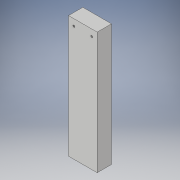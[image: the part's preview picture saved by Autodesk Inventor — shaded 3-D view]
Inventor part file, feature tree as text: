
AUTODESK INVENTOR PART (.ipt)
format: ipt  version: 2019 (Build 230136000, 136)  size: 103,936 bytes
history: native  units: in
note: dims shown in document units (in); Inventor stores cm internally (conversion verified against a paired STEP export)
features: sketch x2, extrude x1, hole x1
ambient origin geometry x8: Origin, YZ Plane, XZ Plane, XY Plane, X Axis, Y Axis, Z Axis, Center Point
bodies: Solid1 (feature_tree)
feature tree (4):
  extrude  "Extrusion1"  Depth=4.25in
  hole  "Hole1"  [1 undecoded]
  sketch  "Sketch1"  dims[d0=1.0in d1=4.25in]
  sketch  "Sketch2"  dims[d2=0.5in d3=0.0in d4=0.625in d5=0.228in d6=0.228in d7=1.0in d8=0.1875in d9=0.067in d10=0.172in d11=0.375in d12=0.25in d13=0.5635in d14=0.261in d15=0.8108in]
note: 1 required parameter value undecoded (feature->parameter linkage not recoverable at this tier; creation-order binding heuristic only, values carry confidence <= 0.55)
